# Revit family: Backflow_Preventer-DC-Zurn_Wilkins-Model_450OSY_450OSYG-(4-6_Inch)
name_source: partatom
category: Pipe Accessories
units: mm (PartAtom-declared; Revit-internal decimal feet)

## family parameters
Always vertical = Yes
Cut with Voids When Loaded = No
OmniClass Number = 23.65.55.14.21
OmniClass Title = Non-Return Valves for Liquid Services
Part Type = Valve - Breaks Into
Round Connector Dimension = Use Radius
Shared = No
Work Plane-Based = No

## types (4) — shared parameters
Assembly Code = D2020300
Bend Radius = 1 1/4"
Bend Radius Outside = 2 3/8"
Default Elevation = 0"
Description = Double Check Valve Assembly
Flow Rate (GPM) = 0 GPM
Hydrostatic Test Pressure = 350.00 psi
Main Material = Paint - Zurn - Blue - Ductile Iron
Manufacturer = Zurn Water, LLC
Manufacturer Brand = Zurn Wilkins
Max Working Water Pressure = 175.00 psi
Max Working Water Temperature = 140 °F
Modified Date = 10/16/2025
Pipe Size = 1"
Product Documentation Link = https://files.zurn.com
Product Installation Sheet URL = https://files.zurn.com
Product Page URL = https://www.zurn.com
Product data URL = https://www.bimobject.com
Repair Parts URL = https://files.zurn.com
URL = https://www.zurn.com

## per-type parameters (varying)
| type | DIM A - Inlet center to outlet center | DIM B - Total height of the valve | DIM C - Center to gate valve stem top | DIM D - Center to cover coupling end | Gate Valve | Height | Length | Main Body | Model | Nominal Diameter | Nominal Radius | Overall Height | Overall Length | Pipe Position | Pipe Vertical Position | Pressure Loss at Rated Flow | Product Weight (lbs) | Rated Flow |
| 4-450OSY (4" 450OSY) | 18 5/16" | 30" | 22 1/2" | 5" | Gate Valve_450(4-6) : 4" | 30" | 18 5/16" | Main Body 450 4&6 : 4" | 450OSY | 4" | 2" | 30" | 18 5/16" | 6 3/8" | 7 1/4" | 5.80 psi | 280 | 500 GPM |
| 4-450OSYG (4" 450OSYG) | 18 5/16" | 30" | 22 1/2" | 5" | Gate Valve_450(4-6) : 4" G | 30" | 18 5/16" | Main Body 450 4&6 : 4" | 450OSYG | 4" | 2" | 30" | 18 5/16" | 6 3/8" | 7 1/4" | 5.80 psi | 260 | 500 GPM |
| 6-450OSYG (6" 450OSYG) | 18 11/16" | 35 1/2" | 30 1/2" | 6 5/16" | Gate Valve_450(4-6) : 6" G | 35 1/2" | 18 11/16" | Main Body 450 4&6 : 6" | 450OSYG | 6" | 3" | 35 1/2" | 18 11/16" | 8 3/4" | 6 1/4" | 4.50 psi | 429 | 1000 GPM |
| 6-450OSY (6" 450OSY) | 18 11/16" | 35 1/2" | 30 1/2" | 6 5/16" | Gate Valve_450(4-6) : 6" | 35 1/2" | 18 11/16" | Main Body 450 4&6 : 6" | 450OSY | 6" | 3" | 35 1/2" | 18 11/16" | 8 3/4" | 6 1/4" | 4.50 psi | 459 | 1000 GPM |

## geometry (parser evidence)
native form markers: Sweep x14
no freeform markers — native parametric forms only
